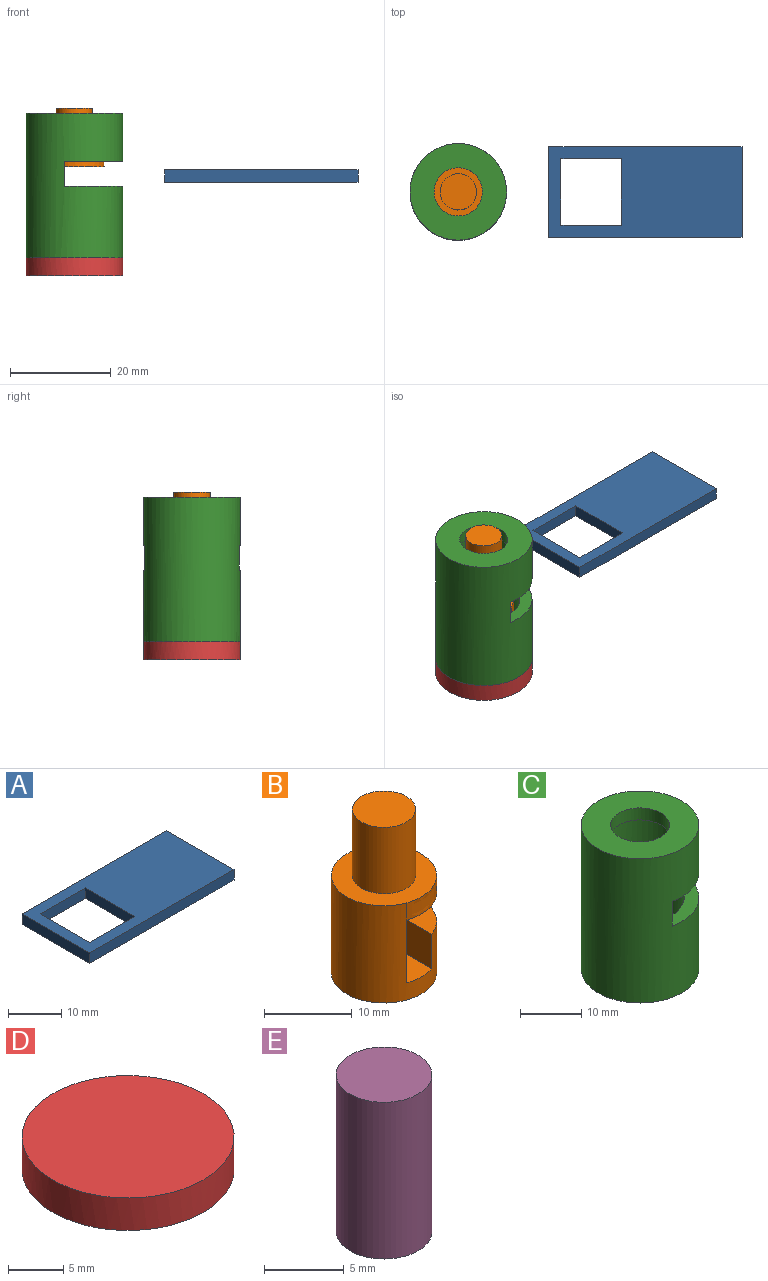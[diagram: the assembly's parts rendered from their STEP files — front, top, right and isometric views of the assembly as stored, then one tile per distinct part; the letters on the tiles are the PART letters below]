
ASSEMBLY  parts=5 mates=4
PART A: 11 faces, bbox 38.4x18x2.4 mm
  f0: plane 13.2x2.4mm, normal (1,0,0), area 31.7mm2, adj f4,f5,f6,f7
  f1: plane 14.41x2.41mm, normal (0,1,0), area 34.6mm2, adj f2,f4,f5,f9
  f2: plane 18x2.4mm, normal (-1,0,0), area 43.2mm2, adj f1,f3,f4,f5
  f3: plane 38.4x2.4mm, normal (0,-1,0), area 92.2mm2, adj f2,f4,f5,f10
  f4: plane 38.4x18.01mm, normal (0,0,1), area 533mm2, adj f0,f1,f2,f3,f6,f7,f8,f9
  f5: plane 38.4x18.01mm, normal (0,0,-1), area 533mm2, adj f0,f1,f2,f3,f6,f7,f8,f9
  f6: plane 12x2.4mm, normal (0,1,0), area 28.8mm2, adj f0,f4,f5,f8
  f7: plane 12x2.4mm, normal (0,-1,0), area 28.8mm2, adj f0,f4,f5,f8
  f8: plane 13.2x2.4mm, normal (-1,0,0), area 31.7mm2, adj f4,f5,f6,f7
  f9: plane 24.01x2.41mm, normal (0,1,0), area 57.6mm2, adj f1,f4,f5,f10
  f10: plane 18.01x2.4mm, normal (1,0,0), area 43.2mm2, adj f3,f4,f5,f9
PART B: 11 faces, bbox 12x12x22.8 mm
  f0: cylinder r=6mm len=13.56mm, axis (0,0,-1), area 327mm2, adj f1,f2,f3,f4,f5,f6,f9
  f1: plane 11.33x8.76mm, normal (1,0,0), area 99.3mm2, adj f0,f3,f7
  f2: plane 11.32x4.01mm, normal (0,0,1), area 33.1mm2, adj f0,f5
  f3: plane 12x3.96mm, normal (0,0,1), area 46.7mm2, adj f0,f1,f5
  f4: plane 12x12mm, normal (0,0,-1), area 113.1mm2, adj f0
  f5: plane 11.32x4.8mm, normal (-1,0,0), area 54.3mm2, adj f0,f2,f3
  f6: extruded ~12x7.97mm, area 54.9mm2, adj f0,f7,f9
  f7: plane 12.01x7.97mm, normal (0,0,-1), area 79.8mm2, adj f1,f6
  f8: cylinder r=3.6mm len=9.24mm, axis (0,0,1), area 209mm2, adj f9,f10
  f9: plane 12.01x12mm, normal (0,0,1), area 72.4mm2, adj f0,f6,f8
  f10: plane 7.2x7.2mm, normal (0,0,1), area 40.7mm2, adj f8
PART C: 11 faces, bbox 19.2x19.2x28.8 mm
  f0: cylinder r=9.6mm len=28.8mm, axis (0,0,1), area 1568mm2, adj f2,f5,f6,f7,f8,f9,f10
  f1: cylinder r=7.2mm len=26.4mm, axis (0,0,-1), area 1062.3mm2, adj f3,f5,f6,f7,f8,f9,f10
  f2: plane 19.2x19.2mm, normal (0,0,1), area 217.1mm2, adj f0,f4
  f3: plane 14.4x14.4mm, normal (0,0,-1), area 90.5mm2, adj f1,f4
  f4: cylinder r=4.8mm len=9.6mm, axis (0,0,1), area 72.4mm2, adj f2,f3
  f5: plane 11.57x9.6mm, normal (0,0,-1), area 36.4mm2, adj f0,f1,f6,f8
  f6: plane 11.57x9.6mm, normal (0,0,-1), area 36.4mm2, adj f0,f1,f5,f9
  f7: plane 19.2x11.57mm, normal (0,0,1), area 72.9mm2, adj f0,f1,f8,f9
  f8: plane 4.97x2.47mm, normal (1,0,0), area 12.3mm2, adj f0,f1,f5,f7
  f9: plane 4.94x2.47mm, normal (1,0,0), area 12.2mm2, adj f0,f1,f6,f7
  f10: plane 19.2x19.2mm, normal (0,0,-1), area 126.7mm2, adj f0,f1
PART D: 3 faces, bbox 19.2x19.2x3.6 mm
  f0: plane 19.2x19.2mm, normal (0,0,1), area 289.5mm2, adj f2
  f1: plane 19.2x19.2mm, normal (0,0,-1), area 289.5mm2, adj f2
  f2: cylinder r=9.6mm len=19.2mm, axis (0,0,1), area 217.1mm2, adj f0,f1
PART E: 3 faces, bbox 6x6x12 mm
  f0: cylinder r=3mm len=12mm, axis (0,0,-1), area 226.2mm2, adj f1,f2
  f1: plane 6x6mm, normal (0,0,1), area 28.3mm2, adj f0
  f2: plane 6x6mm, normal (0,0,-1), area 28.3mm2, adj f0
PLACE A t=(19.23,0,6.68)mm
PLACE B t=(0,0,1)mm
PLACE C t=(0,0,6)mm
PLACE D t=(0,0,6)mm
PLACE E t=(0,0,6)mm
MATE slider E.f0 <-> B.f0  axis (0,0,1) through (0,0,12)mm
MATE fastened E.f0 <-> D.f2  axis (0,0,-1) through (0,0,0)mm
MATE slider A.f2 <-> B.f1  axis (-1,0,0) through (18.03,0,16.28)mm
MATE fastened C.f1 <-> D.f2  axis (0,0,-1) through (0,0,0)mm
